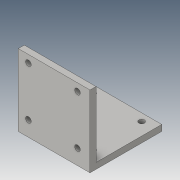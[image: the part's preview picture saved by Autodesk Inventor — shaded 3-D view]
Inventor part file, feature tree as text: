
AUTODESK INVENTOR PART (.ipt)
format: ipt  version: 2016 (Build 200138000, 138)  size: 107,008 bytes
history: native  units: in
note: dims shown in document units (in); Inventor stores cm internally (conversion verified against a paired STEP export)
features: extrude x3, sketch x3, projected_geometry x1
ambient origin geometry x8: Origin, YZ Plane, XZ Plane, XY Plane, X Axis, Y Axis, Z Axis, Center Point
bodies: Solid1 (feature_tree)
feature tree (7):
  extrude  "Extrusion1"  Depth=1.4961in
  extrude  "Extrusion2"  Depth=1.4961in
  extrude  "Extrusion3"  Depth=1.4961in
  sketch  "Sketch1"  dims[d0=0.126in d1=1.4961in]
  sketch  "Sketch2"  dims[d2=0.126in d3=1.4961in]
  projected_geometry  "Projected Loop1"
  sketch  "Sketch3"  dims[d4=1.4961in d5=0.0in d11=0.7874in d13=1.0236in d14=0.7874in d16=1.0236in d19=0.315in d20=0.1181in d21=0.0in d22=0.0in d24=0.7874in d26=0.7874in d27=1.0236in d28=1.0236in d30=0.1181in d31=0.315in d32=0.0in d33=0.0in]
